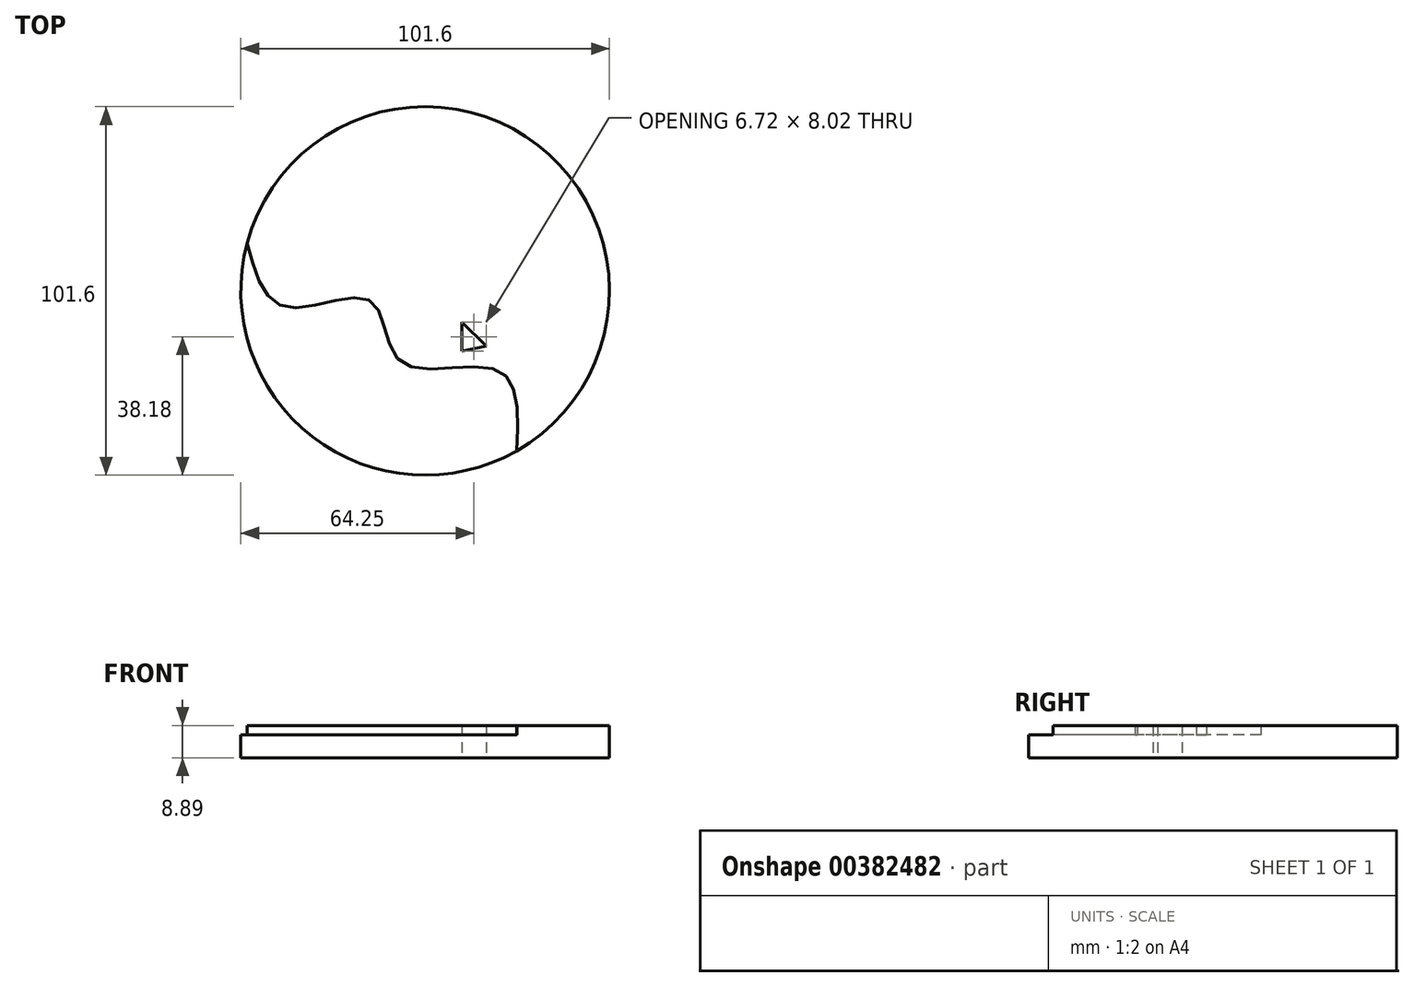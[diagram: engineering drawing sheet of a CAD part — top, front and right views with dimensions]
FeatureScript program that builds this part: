
annotation { "Feature Type Name" : "Feature", "Feature Type Description" : "" }
export const myFeature = defineFeature(function(context is Context, id is Id, definition is map)
    precondition{}
    {
        {
            var Q0;
            Q0=qCreatedBy(makeId("Top.planeOp"),FACE);
            var sketch = newSketch(context, id + "F0", { "sketchPlane" : qUnion([Q0])});
            skCircle(sketch, "E0", {"center": v(-10.1, -3.86) * mm, "radius": 50.8 * mm});
            skFitSpline(sketch, "E1", {"points": [v(-59.15, 9.32) * mm, v(-48.39, -8.32) * mm, v(-25.23, -6.54) * mm, v(-16.62, -23.46) * mm, v(10.1, -25.83) * mm, v(15.1, -47.98) * mm], "startDerivative": vector(34.29, -127.34) * mm, "endDerivative": vector(-7.5, -144.09) * mm});
            skLineSegment(sketch, "E2", {"start": v(3.27, -15.14) * mm, "end": v(24.34, 6.23) * mm});
            skLineSegment(sketch, "E3", {"start": v(0, -12.47) * mm, "end": v(6.72, -19.1) * mm});
            skLineSegment(sketch, "E4", {"start": v(0, -12.47) * mm, "end": v(0, -20.49) * mm});
            skLineSegment(sketch, "E5", {"start": v(0, -20.49) * mm, "end": v(6.72, -19.1) * mm});
            skLineSegment(sketch, "E6", {"start": v(24.34, 6.23) * mm, "end": v(24.34, 11.87) * mm});
            skLineSegment(sketch, "E7", {"start": v(24.34, 6.23) * mm, "end": v(29.06, 11.01) * mm});
            skLineSegment(sketch, "E8", {"start": v(24.34, 6.23) * mm, "end": v(30.87, 6.23) * mm});
            skLineSegment(sketch, "E9", {"start": v(30.87, 6.23) * mm, "end": v(24.34, 6.23) * mm});
            skLineSegment(sketch, "E10", {"start": v(24.34, 6.23) * mm, "end": v(21.2, 9.33) * mm});
            skLineSegment(sketch, "E11", {"start": v(21.2, 9.33) * mm, "end": v(24.34, 6.23) * mm});
            skLineSegment(sketch, "E12", {"start": v(24.34, 6.23) * mm, "end": v(26.88, 3.72) * mm});
            skSolve(sketch);
        }
        {
            var Q0;
            {var subQ0=sQuery(id+"F0.wireOp",EDGE,"E1");Q0=makeQuery(id+"F0.imprint","IMPRINT",FACE,{"disambiguationData":[TD([[makeQuery(id+"F0.imprint","IMPRINT",EDGE,{"derivedFrom":subQ0}),-1.0]])]});}
            extrude(context, id + "F1", {"entities" : qUnion([Q0]), "depth" : 6.35 * mm});
        }
        {
            var Q0;
            {var subQ0=sQuery(id+"F0.wireOp",EDGE,"E1");Q0=makeQuery(id+"F0.imprint","IMPRINT",FACE,{"disambiguationData":[TD([[makeQuery(id+"F0.imprint","IMPRINT",EDGE,{"derivedFrom":subQ0}),1.0]])]});}
            extrude(context, id + "F2", {"entities" : qUnion([Q0]), "operationType" : NewBodyOperationType.ADD, "depth" : 8.9 * mm});
        }
    });
